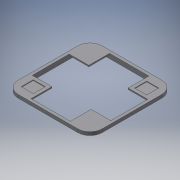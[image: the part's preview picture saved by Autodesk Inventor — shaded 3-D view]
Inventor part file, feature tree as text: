
AUTODESK INVENTOR PART (.ipt)
format: ipt  version: 2016 SP2 (Build 200236200, 236)  size: 183,808 bytes
history: native  units: mm
features: reference x7, extrude x3, sketch x3, chamfer x1
ambient origin geometry x8: Origin, YZ Plane, XZ Plane, XY Plane, X Axis, Y Axis, Z Axis, Center Point
bodies: Volumenkörper1 (feature_tree)
feature tree (14):
  extrude  "Extrusion1"  Depth=3.0mm
  chamfer  "Fase1"  Distance=12.0mm
  extrude  "Extrusion2"  Depth=0.8mm
  extrude  "Extrusion3"  Depth=5.0mm TaperAngle=0.0deg
  sketch  "Skizze1"  dims[d0=0.18mm d1=3.0mm]
  reference  "Referenz1"
  reference  "Referenz2"
  reference  "Referenz3"
  sketch  "Skizze2"  dims[d2=12.0mm]
  reference  "Referenz4"
  reference  "Referenz5"
  sketch  "Skizze3"  dims[d3=12.0mm d4=12.0mm d5=12.0mm d6=5.0mm d7=0.0mm d8=2.0mm d9=2.0mm d10=6.108652mm d11=10.0mm d12=10.0mm d13=10.0mm d14=10.0mm d15=1.4mm d16=0.0mm d17=13.0mm d18=13.0mm d19=13.0mm d20=13.0mm d21=0.8mm d22=0.0mm]
  reference  "Referenz6"
  reference  "Referenz7"
